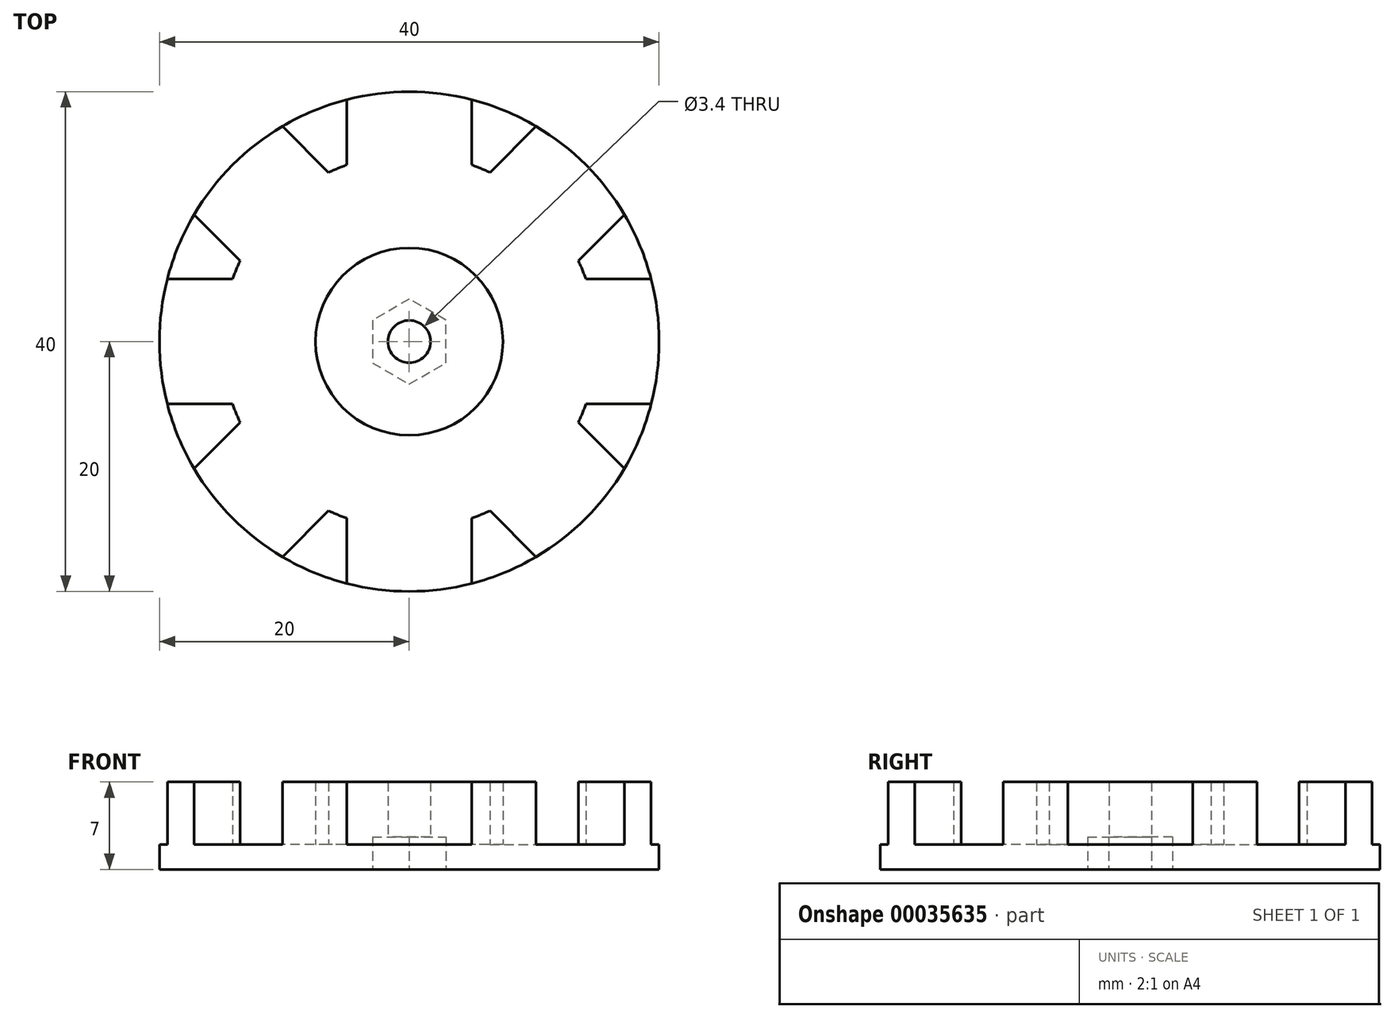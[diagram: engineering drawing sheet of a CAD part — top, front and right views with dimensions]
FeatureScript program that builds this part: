
annotation { "Feature Type Name" : "Feature", "Feature Type Description" : "" }
export const myFeature = defineFeature(function(context is Context, id is Id, definition is map)
    precondition{}
    {
        {
            var Q0;
            Q0=qCreatedBy(makeId("Top.planeOp"),FACE);
            var sketch = newSketch(context, id + "F0", { "sketchPlane" : qUnion([Q0])});
            skCircle(sketch, "E0", {"center": v(0, 0) * mm, "radius": 20 * mm});
            skCircle(sketch, "E1", {"center": v(0, 0) * mm, "radius": 1.7 * mm});
            skSolve(sketch);
        }
        {
            var Q0;
            Q0=makeQuery(id+"F0.imprint","IMPRINT",FACE,{"disambiguationData":[TD([[makeQuery(id+"F0.imprint","IMPRINT",EDGE,{"derivedFrom":sQuery(id+"F0.wireOp",EDGE,"E0")}),1.0]])]});
            extrude(context, id + "F1", {"entities" : qUnion([Q0]), "depth" : 2 * mm});
        }
        {
            var Q0;
            Q0=makeQuery(id+"F1.opExtrude","CAP_FACE",FACE,{"disambiguationData":[OSD([sQuery(id+"F0.wireOp",EDGE,"E0"),sQuery(id+"F0.wireOp",EDGE,"E1")])],"isStart":false});
            var sketch = newSketch(context, id + "F2", { "sketchPlane" : qUnion([Q0])});
            skCircle(sketch, "E2.0", {"center": v(0, 0) * mm, "radius": 20 * mm});
            skCircle(sketch, "E3", {"center": v(0, 0) * mm, "radius": 15 * mm});
            skCircle(sketch, "E4", {"center": v(0, 0) * mm, "radius": 7.5 * mm});
            skSolve(sketch);
        }
        {
            var Q0;
            Q0=makeQuery(id+"F2.imprint","IMPRINT",FACE,{"disambiguationData":[TD([[makeQuery(id+"F2.imprint","IMPRINT",EDGE,{"derivedFrom":sQuery(id+"F2.wireOp",EDGE,"E4")}),1.0]])]});
            var Q1;
            Q1=makeQuery(id+"F2.imprint","IMPRINT",FACE,{"disambiguationData":[TD([[makeQuery(id+"F2.imprint","IMPRINT",EDGE,{"derivedFrom":sQuery(id+"F2.wireOp",EDGE,"E2.0")}),1.0]])]});
            extrude(context, id + "F3", {"entities" : qUnion([Q0, Q1]), "operationType" : NewBodyOperationType.ADD, "depth" : 5 * mm});
        }
        {
            var Q0;
            Q0=makeQuery(id+"F3.opExtrude","CAP_FACE",FACE,{"disambiguationData":[OSD([sQuery(id+"F2.wireOp",EDGE,"E2.0"),sQuery(id+"F2.wireOp",EDGE,"E3")])],"isStart":false});
            var sketch = newSketch(context, id + "F4", { "sketchPlane" : qUnion([Q0])});
            skLineSegment(sketch, "E5.bottom", {"start": v(-23, -5) * mm, "end": v(-13, -5) * mm});
            skLineSegment(sketch, "E5.top", {"start": v(-23, 5) * mm, "end": v(-13, 5) * mm});
            skLineSegment(sketch, "E5.left", {"start": v(-23, -5) * mm, "end": v(-23, 5) * mm});
            skLineSegment(sketch, "E5.right", {"start": v(-13, -5) * mm, "end": v(-13, 5) * mm});
            skLineSegment(sketch, "E6", {"start": v(-25.06, 0) * mm, "end": v(22.26, 0) * mm, "construction": true});
            skLineSegment(sketch, "E7.1.0", {"start": v(-19.8, -12.73) * mm, "end": v(-12.73, -5.66) * mm});
            skLineSegment(sketch, "E7.1.1", {"start": v(-12.73, -19.8) * mm, "end": v(-19.8, -12.73) * mm});
            skLineSegment(sketch, "E7.1.2", {"start": v(-12.73, -19.8) * mm, "end": v(-5.66, -12.73) * mm});
            skLineSegment(sketch, "E7.1.3", {"start": v(-5.66, -12.73) * mm, "end": v(-12.73, -5.66) * mm});
            skLineSegment(sketch, "E7.2.0", {"start": v(-5, -23) * mm, "end": v(-5, -13) * mm});
            skLineSegment(sketch, "E7.2.1", {"start": v(5, -23) * mm, "end": v(-5, -23) * mm});
            skLineSegment(sketch, "E7.2.2", {"start": v(5, -23) * mm, "end": v(5, -13) * mm});
            skLineSegment(sketch, "E7.2.3", {"start": v(5, -13) * mm, "end": v(-5, -13) * mm});
            skLineSegment(sketch, "E7.3.0", {"start": v(12.73, -19.8) * mm, "end": v(5.66, -12.73) * mm});
            skLineSegment(sketch, "E7.3.1", {"start": v(19.8, -12.73) * mm, "end": v(12.73, -19.8) * mm});
            skLineSegment(sketch, "E7.3.2", {"start": v(19.8, -12.73) * mm, "end": v(12.73, -5.66) * mm});
            skLineSegment(sketch, "E7.3.3", {"start": v(12.73, -5.66) * mm, "end": v(5.66, -12.73) * mm});
            skLineSegment(sketch, "E7.4.0", {"start": v(23, -5) * mm, "end": v(13, -5) * mm});
            skLineSegment(sketch, "E7.4.1", {"start": v(23, 5) * mm, "end": v(23, -5) * mm});
            skLineSegment(sketch, "E7.4.2", {"start": v(23, 5) * mm, "end": v(13, 5) * mm});
            skLineSegment(sketch, "E7.4.3", {"start": v(13, 5) * mm, "end": v(13, -5) * mm});
            skLineSegment(sketch, "E7.5.0", {"start": v(19.8, 12.73) * mm, "end": v(12.73, 5.66) * mm});
            skLineSegment(sketch, "E7.5.1", {"start": v(12.73, 19.8) * mm, "end": v(19.8, 12.73) * mm});
            skLineSegment(sketch, "E7.5.2", {"start": v(12.73, 19.8) * mm, "end": v(5.66, 12.73) * mm});
            skLineSegment(sketch, "E7.5.3", {"start": v(5.66, 12.73) * mm, "end": v(12.73, 5.66) * mm});
            skLineSegment(sketch, "E7.6.0", {"start": v(5, 23) * mm, "end": v(5, 13) * mm});
            skLineSegment(sketch, "E7.6.1", {"start": v(-5, 23) * mm, "end": v(5, 23) * mm});
            skLineSegment(sketch, "E7.6.2", {"start": v(-5, 23) * mm, "end": v(-5, 13) * mm});
            skLineSegment(sketch, "E7.6.3", {"start": v(-5, 13) * mm, "end": v(5, 13) * mm});
            skLineSegment(sketch, "E7.7.0", {"start": v(-12.73, 19.8) * mm, "end": v(-5.66, 12.73) * mm});
            skLineSegment(sketch, "E7.7.1", {"start": v(-19.8, 12.73) * mm, "end": v(-12.73, 19.8) * mm});
            skLineSegment(sketch, "E7.7.2", {"start": v(-19.8, 12.73) * mm, "end": v(-12.73, 5.66) * mm});
            skLineSegment(sketch, "E7.7.3", {"start": v(-12.73, 5.66) * mm, "end": v(-5.66, 12.73) * mm});
            skPoint(sketch, "E7.center", {"position": v(0, 0) * mm});
            skSolve(sketch);
        }
        {
            var Q0;
            Q0 = qSketchRegion(id + "F4", true);
            var Q1;
            Q1=makeQuery(id+"F1.opExtrude","CAP_FACE",FACE,{"disambiguationData":[OSD([sQuery(id+"F0.wireOp",EDGE,"E0"),sQuery(id+"F0.wireOp",EDGE,"E1")])],"isStart":false});
            extrude(context, id + "F5", {"entities" : qUnion([Q0]), "operationType" : NewBodyOperationType.REMOVE, "endBound" : BoundingType.UP_TO_SURFACE, "oppositeDirection" : true, "endBoundEntityFace" : qUnion([Q1]), "depth" : 25 * mm});
        }
        {
            var Q0;
            Q0=makeQuery(id+"F1.opExtrude","CAP_FACE",FACE,{"disambiguationData":[OSD([sQuery(id+"F0.wireOp",EDGE,"E0"),sQuery(id+"F0.wireOp",EDGE,"E1")])],"isStart":true});
            var sketch = newSketch(context, id + "F6", { "sketchPlane" : qUnion([Q0])});
            skCircle(sketch, "E8.cCircle", {"center": v(0, 0) * mm, "radius": 2.95 * mm, "construction": true});
            skLineSegment(sketch, "E8.0", {"start": v(2.95, 1.7) * mm, "end": v(2.95, -1.7) * mm});
            skLineSegment(sketch, "E8.1", {"start": v(2.95, -1.7) * mm, "end": v(0, -3.4) * mm});
            skLineSegment(sketch, "E8.2", {"start": v(0, -3.4) * mm, "end": v(-2.95, -1.7) * mm});
            skLineSegment(sketch, "E8.3", {"start": v(-2.95, -1.7) * mm, "end": v(-2.95, 1.7) * mm});
            skLineSegment(sketch, "E8.4", {"start": v(-2.95, 1.7) * mm, "end": v(0, 3.4) * mm});
            skLineSegment(sketch, "E8.5", {"start": v(0, 3.4) * mm, "end": v(2.95, 1.7) * mm});
            skPoint(sketch, "E8.0.midPoint", {"position": v(2.95, 0) * mm});
            skSolve(sketch);
        }
        {
            var Q0;
            Q0=makeQuery(id+"F6.imprint","IMPRINT",FACE,{"disambiguationData":[TD([[makeQuery(id+"F6.imprint","IMPRINT",EDGE,{"derivedFrom":sQuery(id+"F6.wireOp",EDGE,"E8.0")}),-1.0]])]});
            extrude(context, id + "F7", {"entities" : qUnion([Q0]), "operationType" : NewBodyOperationType.REMOVE, "oppositeDirection" : true, "depth" : 2.6 * mm});
        }
    });
